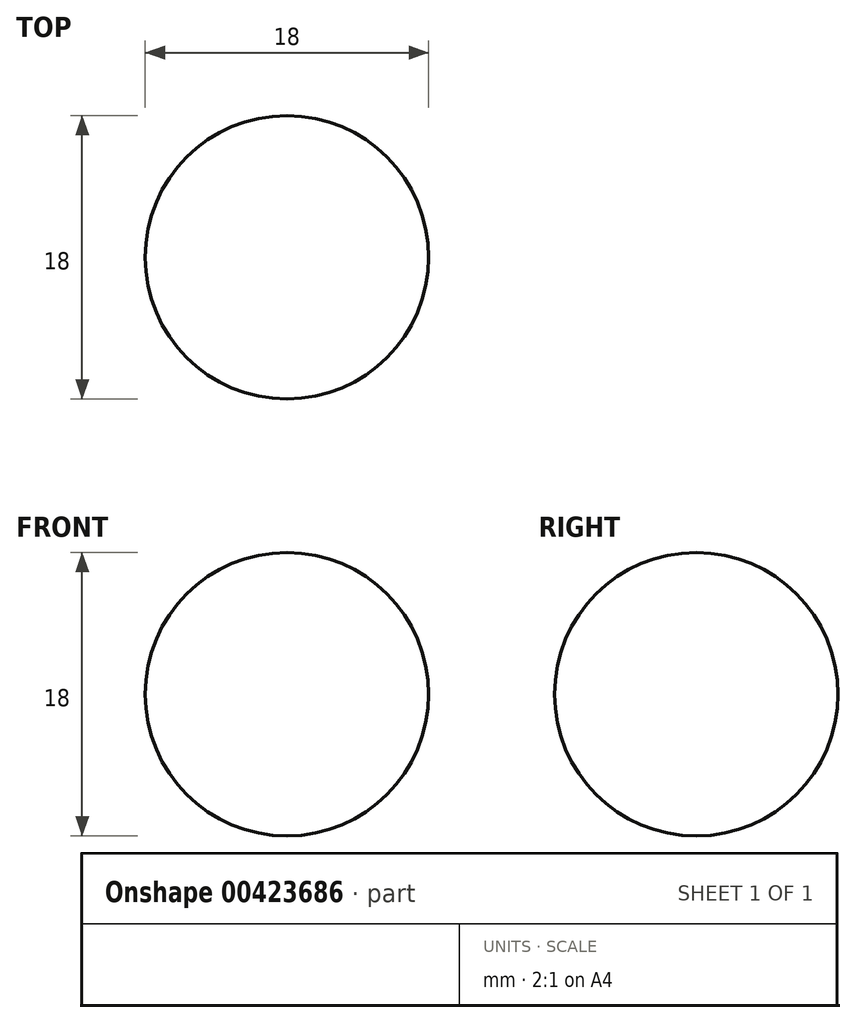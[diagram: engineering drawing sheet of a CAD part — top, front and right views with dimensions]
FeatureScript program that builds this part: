
annotation { "Feature Type Name" : "Feature", "Feature Type Description" : "" }
export const myFeature = defineFeature(function(context is Context, id is Id, definition is map)
    precondition{}
    {
        {
            var Q0;
            Q0=qCreatedBy(makeId("Right.planeOp"),FACE);
            var sketch = newSketch(context, id + "F0", { "sketchPlane" : qUnion([Q0])});
            skLineSegment(sketch, "E0", {"start": v(0, 9) * mm, "end": v(0, -9) * mm});
            skArc(sketch, "E1", {"start": v(0, -9) * mm, "mid": v(9, 0) * mm, "end": v(0, 9) * mm});
            skSolve(sketch);
        }
        {
            var Q0;
            Q0=makeQuery(id+"F0.imprint","IMPRINT",FACE,{"disambiguationData":[TD([[makeQuery(id+"F0.imprint","IMPRINT",EDGE,{"derivedFrom":sQuery(id+"F0.wireOp",EDGE,"E0")}),1.0]])]});
            var Q1;
            Q1=sQuery(id+"F0.wireOp",EDGE,"E0");
            revolve(context, id + "F1", {"entities" : qUnion([Q0]), "axis" : qUnion([Q1]), "revolveType" : RevolveType.FULL});
        }
    });
